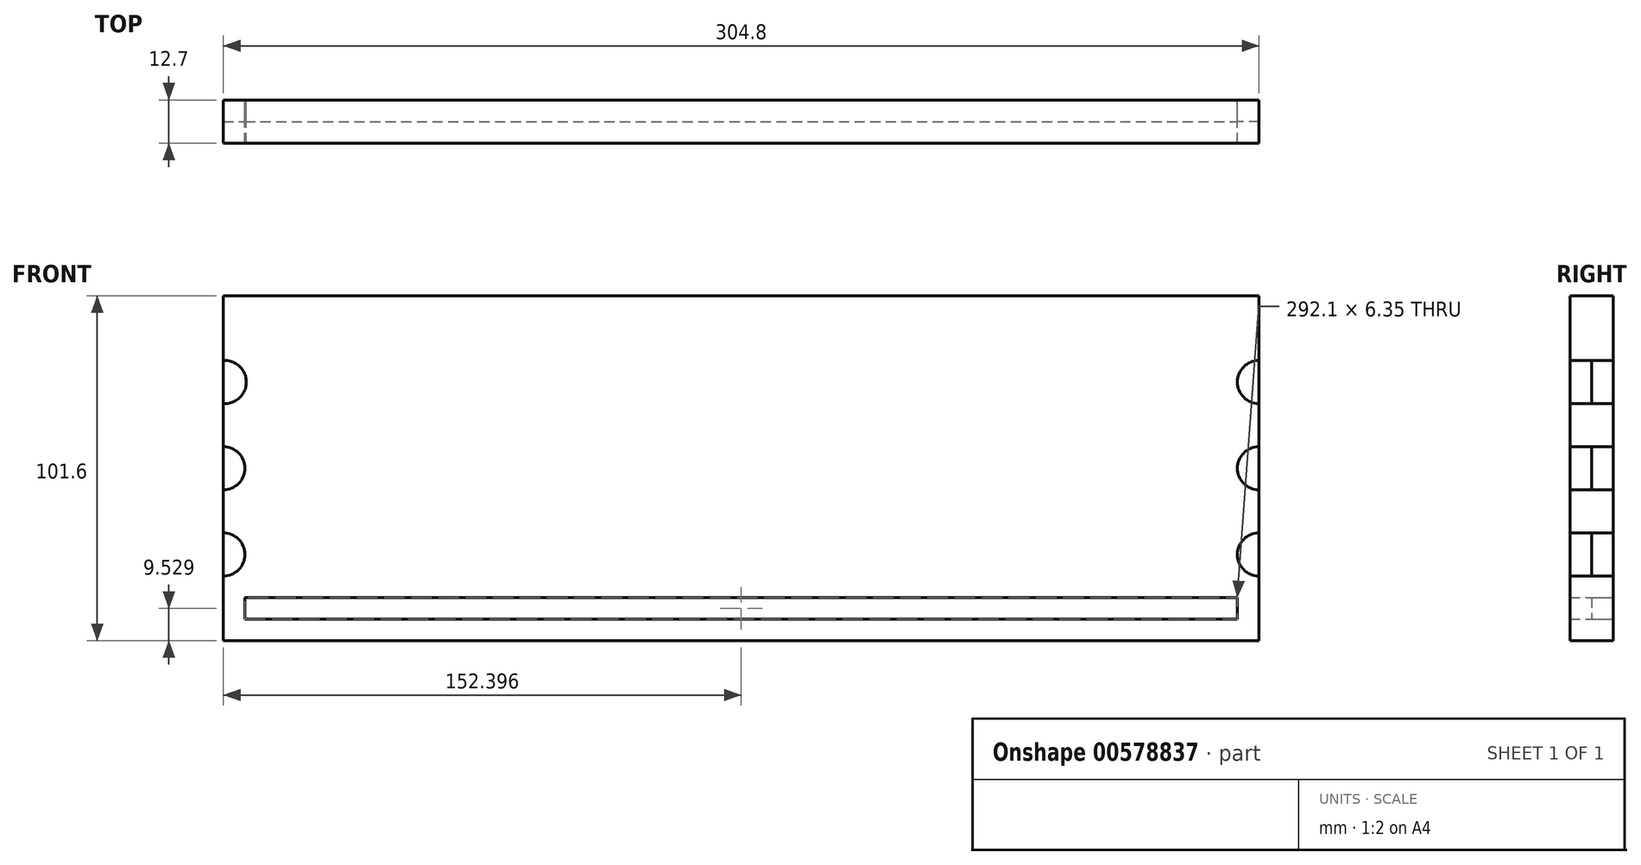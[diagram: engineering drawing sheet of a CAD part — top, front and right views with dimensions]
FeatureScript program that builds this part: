
annotation { "Feature Type Name" : "Feature", "Feature Type Description" : "" }
export const myFeature = defineFeature(function(context is Context, id is Id, definition is map)
    precondition{}
    {
        {
            var Q0;
            Q0=qCreatedBy(makeId("Front.planeOp"),FACE);
            var sketch = newSketch(context, id + "F0", { "sketchPlane" : qUnion([Q0])});
            skLineSegment(sketch, "E0.bottom", {"start": v(-88.31, 66.7) * mm, "end": v(216.49, 66.7) * mm});
            skLineSegment(sketch, "E0.top", {"start": v(-88.31, -34.9) * mm, "end": v(216.49, -34.9) * mm});
            skLineSegment(sketch, "E0.left", {"start": v(-88.31, 66.7) * mm, "end": v(-88.31, -34.9) * mm});
            skLineSegment(sketch, "E0.right", {"start": v(216.49, 66.7) * mm, "end": v(216.49, -34.9) * mm});
            skArc(sketch, "E1", {"start": v(-88.31, 34.94) * mm, "mid": v(-81.56, 41.3) * mm, "end": v(-88.31, 47.64) * mm});
            skArc(sketch, "E2", {"start": v(-88.31, 9.54) * mm, "mid": v(-81.96, 15.9) * mm, "end": v(-88.31, 22.24) * mm});
            skArc(sketch, "E3", {"start": v(-88.31, -15.86) * mm, "mid": v(-81.96, -9.5) * mm, "end": v(-88.31, -3.16) * mm});
            skArc(sketch, "E4", {"start": v(216.49, 47.64) * mm, "mid": v(210.14, 41.3) * mm, "end": v(216.49, 34.94) * mm});
            skArc(sketch, "E5", {"start": v(216.49, 22.24) * mm, "mid": v(210.14, 15.9) * mm, "end": v(216.49, 9.54) * mm});
            skArc(sketch, "E6", {"start": v(216.49, -3.16) * mm, "mid": v(210.14, -9.5) * mm, "end": v(216.49, -15.86) * mm});
            skLineSegment(sketch, "E7.bottom", {"start": v(-81.96, -22.2) * mm, "end": v(210.14, -22.2) * mm});
            skLineSegment(sketch, "E7.top", {"start": v(-81.96, -28.56) * mm, "end": v(210.14, -28.56) * mm});
            skLineSegment(sketch, "E7.left", {"start": v(-81.96, -22.2) * mm, "end": v(-81.96, -28.56) * mm});
            skLineSegment(sketch, "E7.right", {"start": v(210.14, -22.2) * mm, "end": v(210.14, -28.56) * mm});
            skSolve(sketch);
        }
        {
            var Q0;
            Q0=makeQuery(id+"F0.imprint","IMPRINT",FACE,{"disambiguationData":[TD([[makeQuery(id+"F0.imprint","IMPRINT",EDGE,{"derivedFrom":sQuery(id+"F0.wireOp",EDGE,"E7.bottom")}),-1.0]])]});
            extrude(context, id + "F1", {"entities" : qUnion([Q0]), "depth" : 6.35 * mm, "offsetDistance" : 25.4 * mm});
        }
        {
            var Q0;
            {var subQ0=sQuery(id+"F0.wireOp",EDGE,"E3");Q0=makeQuery(id+"F0.imprint","IMPRINT",FACE,{"disambiguationData":[TD([[makeQuery(id+"F0.imprint","IMPRINT",EDGE,{"derivedFrom":subQ0}),1.0]])]});}
            var Q1;
            {var subQ0=sQuery(id+"F0.wireOp",EDGE,"E2");Q1=makeQuery(id+"F0.imprint","IMPRINT",FACE,{"disambiguationData":[TD([[makeQuery(id+"F0.imprint","IMPRINT",EDGE,{"derivedFrom":subQ0}),1.0]])]});}
            var Q2;
            {var subQ0=sQuery(id+"F0.wireOp",EDGE,"E1");Q2=makeQuery(id+"F0.imprint","IMPRINT",FACE,{"disambiguationData":[TD([[makeQuery(id+"F0.imprint","IMPRINT",EDGE,{"derivedFrom":subQ0}),1.0]])]});}
            var Q3;
            {var subQ0=sQuery(id+"F0.wireOp",EDGE,"E4");Q3=makeQuery(id+"F0.imprint","IMPRINT",FACE,{"disambiguationData":[TD([[makeQuery(id+"F0.imprint","IMPRINT",EDGE,{"derivedFrom":subQ0}),1.0]])]});}
            var Q4;
            {var subQ0=sQuery(id+"F0.wireOp",EDGE,"E5");Q4=makeQuery(id+"F0.imprint","IMPRINT",FACE,{"disambiguationData":[TD([[makeQuery(id+"F0.imprint","IMPRINT",EDGE,{"derivedFrom":subQ0}),1.0]])]});}
            var Q5;
            {var subQ0=sQuery(id+"F0.wireOp",EDGE,"E6");Q5=makeQuery(id+"F0.imprint","IMPRINT",FACE,{"disambiguationData":[TD([[makeQuery(id+"F0.imprint","IMPRINT",EDGE,{"derivedFrom":subQ0}),1.0]])]});}
            extrude(context, id + "F2", {"entities" : qUnion([Q0, Q1, Q2, Q3, Q4, Q5]), "depth" : 6.35 * mm, "offsetDistance" : 25.4 * mm});
        }
        {
            var Q0;
            {var subQ1=sQuery(id+"F0.wireOp",EDGE,"E0.bottom");Q0=makeQuery(id+"F0.imprint","IMPRINT",FACE,{"disambiguationData":[TD([[makeQuery(id+"F0.imprint","IMPRINT",EDGE,{"derivedFrom":subQ1}),-1.0]])]});}
            var Q1;
            Q1=makeQuery(id+"F2.opExtrude","SWEPT_BODY",BODY,{"disambiguationData":[OSD([sQuery(id+"F0.wireOp",EDGE,"E0.right"),sQuery(id+"F0.wireOp",EDGE,"E4")])]});
            extrude(context, id + "F3", {"entities" : qUnion([Q0]), "depth" : 12.7 * mm, "endBoundEntityBody" : qUnion([Q1]), "offsetDistance" : 25.4 * mm});
        }
    });
